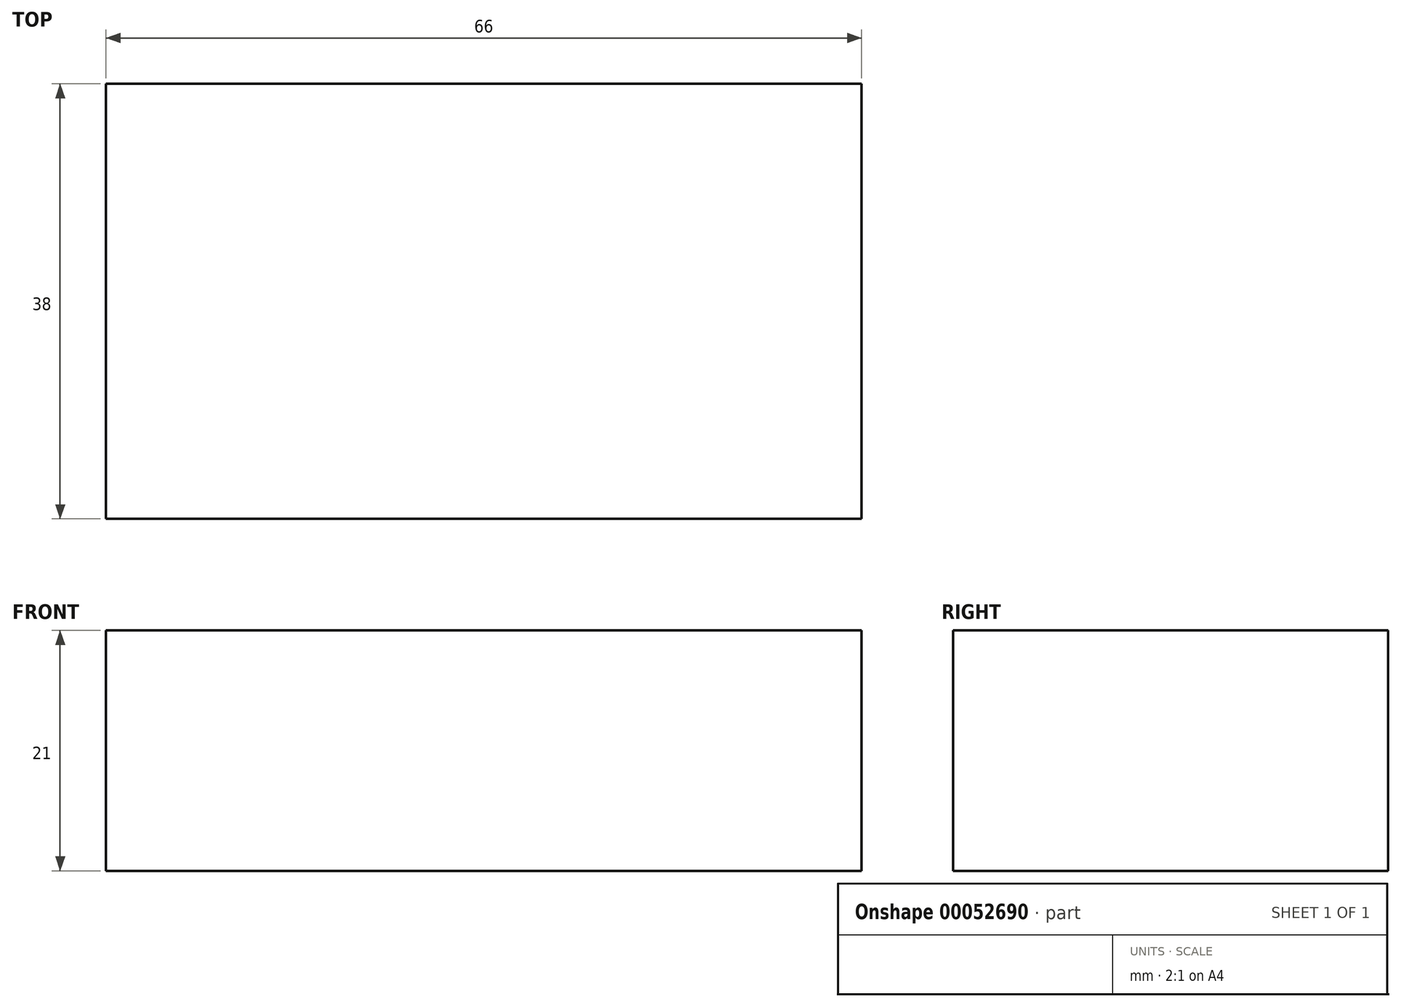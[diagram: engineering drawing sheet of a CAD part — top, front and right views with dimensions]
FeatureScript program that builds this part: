
annotation { "Feature Type Name" : "Feature", "Feature Type Description" : "" }
export const myFeature = defineFeature(function(context is Context, id is Id, definition is map)
    precondition{}
    {
        {
            var Q0;
            Q0=qCreatedBy(makeId("Top.planeOp"),FACE);
            var sketch = newSketch(context, id + "F0", { "sketchPlane" : qUnion([Q0])});
            skLineSegment(sketch, "E0.bottom", {"start": v(-33, 19) * mm, "end": v(33, 19) * mm});
            skLineSegment(sketch, "E0.top", {"start": v(-33, -19) * mm, "end": v(33, -19) * mm});
            skLineSegment(sketch, "E0.left", {"start": v(-33, 19) * mm, "end": v(-33, -19) * mm});
            skLineSegment(sketch, "E0.right", {"start": v(33, 19) * mm, "end": v(33, -19) * mm});
            skSolve(sketch);
        }
        {
            var Q0;
            Q0 = qSketchRegion(id + "F0", true);
            extrude(context, id + "F1", {"entities" : qUnion([Q0]), "depth" : 21 * mm});
        }
    });
